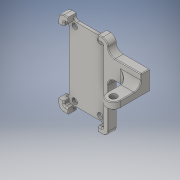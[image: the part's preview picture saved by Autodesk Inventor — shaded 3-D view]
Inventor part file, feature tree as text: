
AUTODESK INVENTOR PART (.ipt)
format: ipt  version: 2016 (Build 200138000, 138)  size: 325,632 bytes
history: native  units: in
note: dims shown in document units (in); Inventor stores cm internally (conversion verified against a paired STEP export)
features: fillet x6, extrude x5, sketch x4
ambient origin geometry x8: Origin, YZ Plane, XZ Plane, XY Plane, X Axis, Y Axis, Z Axis, Center Point
bodies: Solid1 (feature_tree)
feature tree (15):
  sketch  "Sketch1"  dims[d0=2.65in d1=1.4in]
  extrude  "Extrusion1"  Depth=1.4in
  extrude  "Extrusion2"  Depth=0.2in
  fillet  "Fillet1"  [1 undecoded]
  fillet  "Fillet2"  [1 undecoded]
  fillet  "Fillet3"  Radius=0.15in
  extrude  "Extrusion3"  Depth=0.7in
  fillet  "Fillet4"  Radius=1.325in
  extrude  "Extrusion4"  Depth=0.025in
  fillet  "Fillet5"  Radius=0.2in
  extrude  "Extrusion5"  Depth=0.2in
  fillet  "Fillet6"  Radius=0.05in
  sketch  "Sketch2"  dims[d2=0.2in d3=0.2in d4=0.0in d5=0.0in d6=0.15in]
  sketch  "Sketch3"  dims[d7=0.15in d8=0.7in d9=1.325in]
  sketch  "Sketch4"  dims[d10=0.05in d11=0.18in d12=0.2in d13=0.2in d14=0.05in d15=0.1in d16=0.1in d17=0.0in d18=0.3in d19=0.0in d20=0.125in d21=0.05in d22=0.05in d23=0.7in d24=0.25in d25=1.2in d26=0.3in d27=0.0in d28=0.25in d29=0.25in d30=1.0in d31=0.5in d32=0.0in d33=0.25in d34=0.25in d35=0.5in d36=0.0in d37=0.025in]
note: 2 required parameter values undecoded (feature->parameter linkage not recoverable at this tier; creation-order binding heuristic only, values carry confidence <= 0.55)
